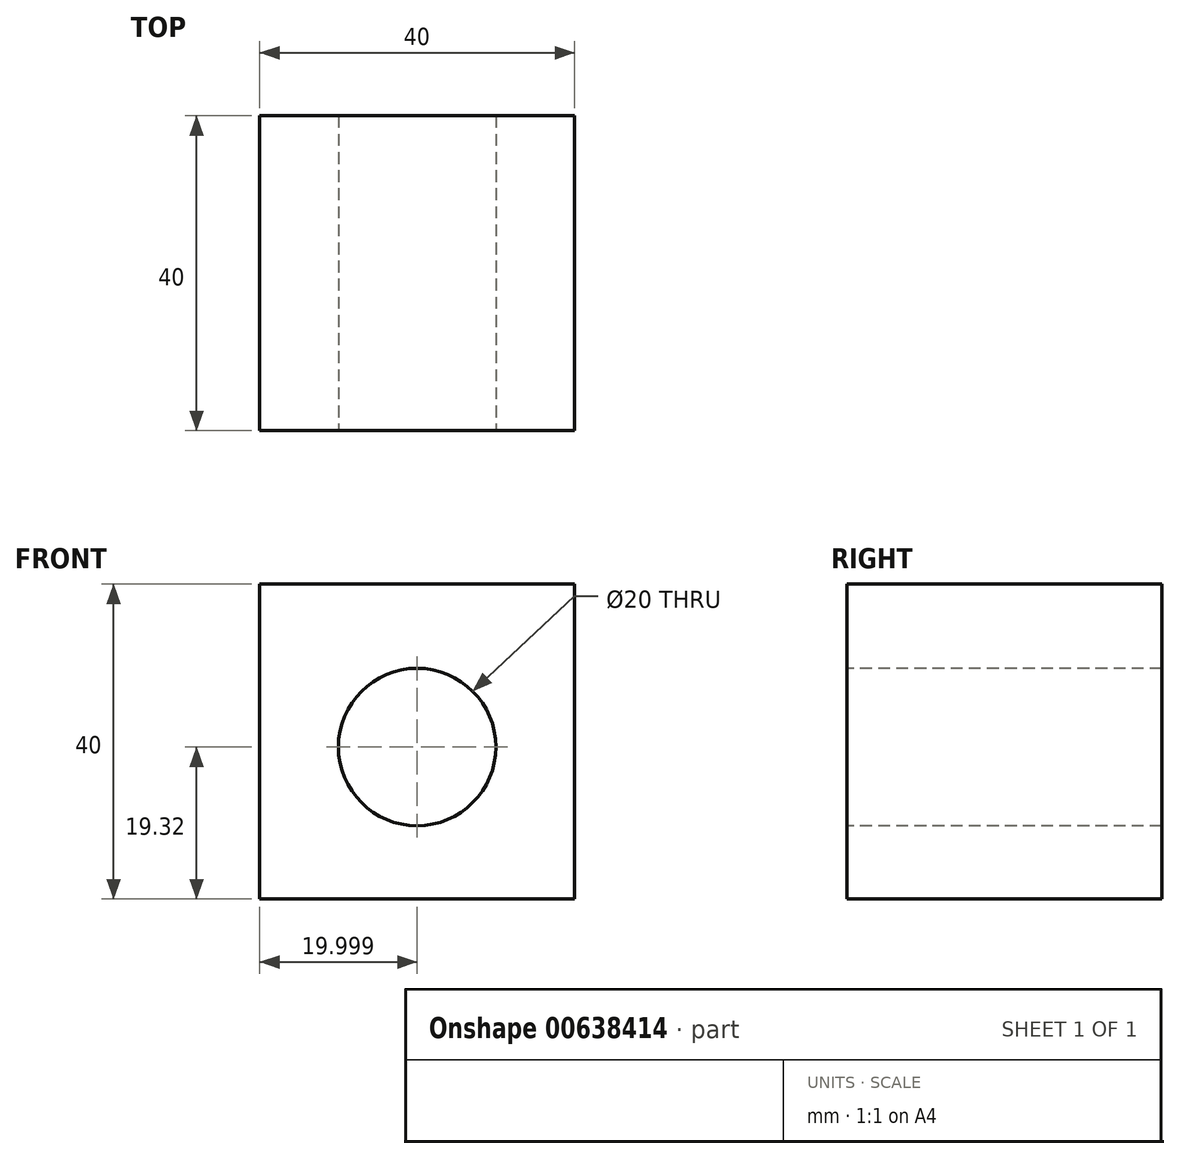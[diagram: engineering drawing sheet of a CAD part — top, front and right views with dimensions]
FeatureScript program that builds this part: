
annotation { "Feature Type Name" : "Feature", "Feature Type Description" : "" }
export const myFeature = defineFeature(function(context is Context, id is Id, definition is map)
    precondition{}
    {
        {
            var Q0;
            Q0=qCreatedBy(makeId("Front.planeOp"),FACE);
            var sketch = newSketch(context, id + "F0", { "sketchPlane" : qUnion([Q0])});
            skLineSegment(sketch, "E0.bottom", {"start": v(-17.32, 20.68) * mm, "end": v(22.68, 20.68) * mm});
            skLineSegment(sketch, "E0.top", {"start": v(-17.32, -19.32) * mm, "end": v(22.68, -19.32) * mm});
            skLineSegment(sketch, "E0.left", {"start": v(-17.32, 20.68) * mm, "end": v(-17.32, -19.32) * mm});
            skLineSegment(sketch, "E0.right", {"start": v(22.68, 20.68) * mm, "end": v(22.68, -19.32) * mm});
            skSolve(sketch);
        }
        {
            var Q0;
            Q0=makeQuery(id+"F0.imprint","IMPRINT",FACE,{"disambiguationData":[TD([[makeQuery(id+"F0.imprint","IMPRINT",EDGE,{"derivedFrom":sQuery(id+"F0.wireOp",EDGE,"E0.bottom")}),-1.0]])]});
            extrude(context, id + "F1", {"entities" : qUnion([Q0]), "depth" : 40 * mm, "offsetDistance" : 25 * mm});
        }
        {
            var Q0;
            Q0=makeQuery(id+"F1.opExtrude","CAP_FACE",FACE,{"disambiguationData":[OSD([sQuery(id+"F0.wireOp",EDGE,"E0.bottom"),sQuery(id+"F0.wireOp",EDGE,"E0.top"),sQuery(id+"F0.wireOp",EDGE,"E0.left"),sQuery(id+"F0.wireOp",EDGE,"E0.right")])],"isStart":false});
            var sketch = newSketch(context, id + "F2", { "sketchPlane" : qUnion([Q0])});
            skCircle(sketch, "E1", {"center": v(2.68, 0) * mm, "radius": 10 * mm});
            skPoint(sketch, "E1.centerSnap0", {"position": v(2.68, 20.68) * mm});
            skSolve(sketch);
        }
        {
            var Q0;
            Q0=sQuery(id+"F2.wireOp",VERTEX,"eVXhWX6A-Pi0i-kj18-dQdj-SuQXque83OXj.center");
            var Q1;
            Q1=sQuery(id+"F2.wireOp",VERTEX,"E1.center");
            var Q2;
            Q2=makeQuery(id+"F1.opExtrude","SWEPT_BODY",BODY,{"disambiguationData":[OSD([sQuery(id+"F0.wireOp",EDGE,"E0.bottom"),sQuery(id+"F0.wireOp",EDGE,"E0.top"),sQuery(id+"F0.wireOp",EDGE,"E0.left"),sQuery(id+"F0.wireOp",EDGE,"E0.right")])]});
            hole(context, id + "F3", {"style" : HoleStyle.SIMPLE, "endStyle" : HoleEndStyle.THROUGH, "holeDiameter" : 20 * mm, "majorDiameter" : 5 * mm, "isTappedThrough" : true, "tappedDepth" : 12 * mm, "tapClearance" : 3, "locations" : qUnion([Q0, Q1]), "scope" : qUnion([Q2])});
        }
    });
